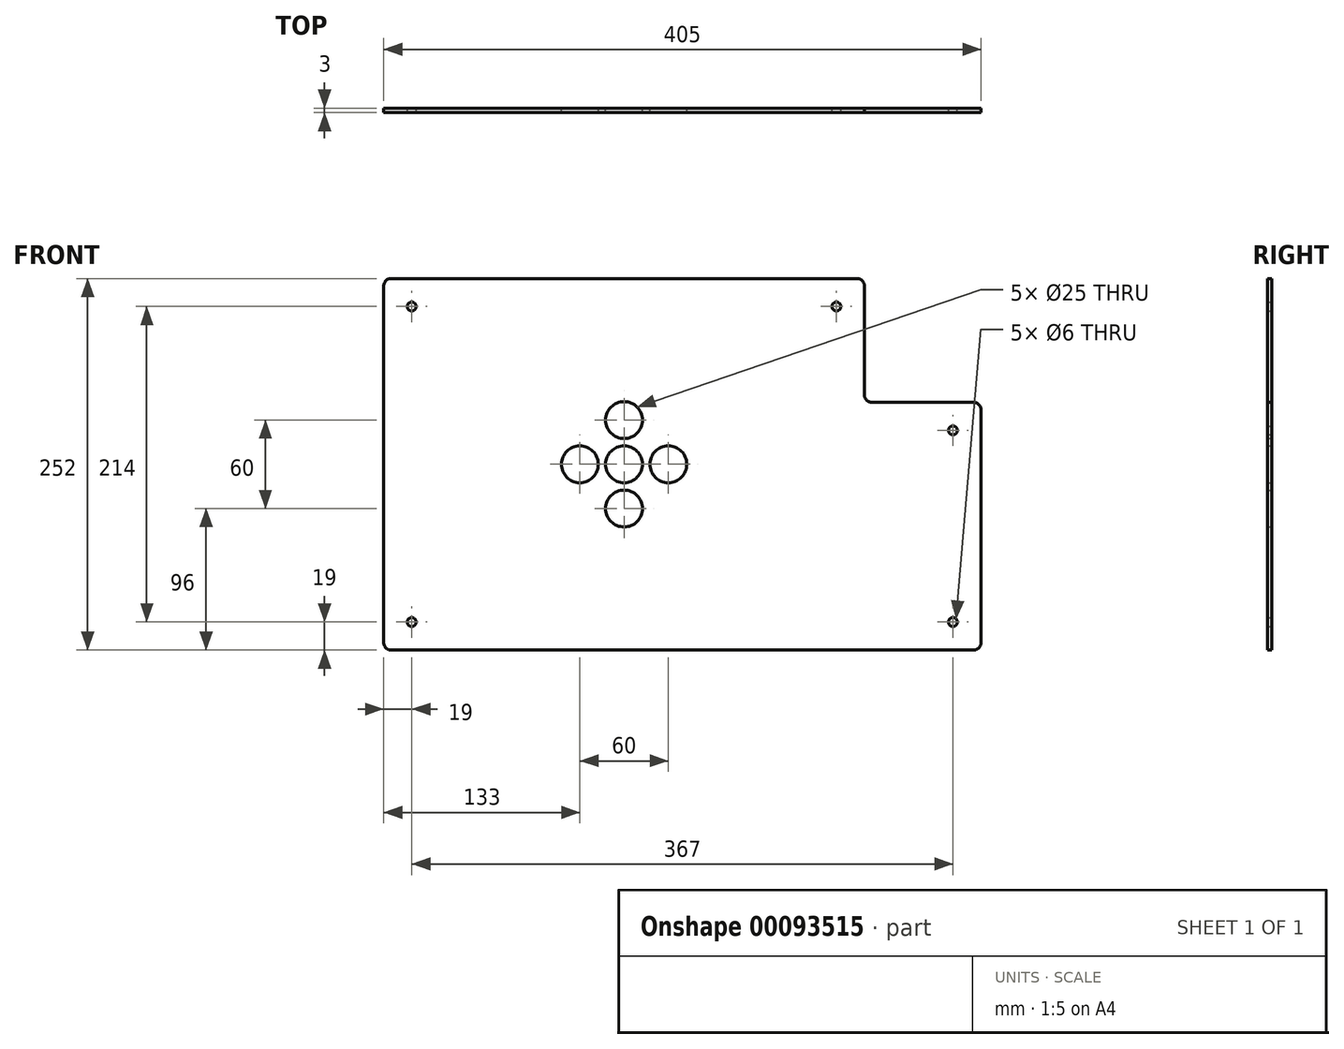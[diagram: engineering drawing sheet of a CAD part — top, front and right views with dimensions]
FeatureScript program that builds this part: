
annotation { "Feature Type Name" : "Feature", "Feature Type Description" : "" }
export const myFeature = defineFeature(function(context is Context, id is Id, definition is map)
    precondition{}
    {
        {
            var Q0;
            Q0=qCreatedBy(makeId("Front.planeOp"),FACE);
            var sketch = newSketch(context, id + "F0", { "sketchPlane" : qUnion([Q0])});
            skLineSegment(sketch, "E0", {"start": v(0, 0) * mm, "end": v(0, 252) * mm});
            skLineSegment(sketch, "E1", {"start": v(0, 0) * mm, "end": v(405, 0) * mm});
            skLineSegment(sketch, "E2", {"start": v(405, 0) * mm, "end": v(405, 168) * mm});
            skLineSegment(sketch, "E3", {"start": v(405, 168) * mm, "end": v(326, 168) * mm});
            skLineSegment(sketch, "E4", {"start": v(326, 168) * mm, "end": v(326, 252) * mm});
            skLineSegment(sketch, "E5", {"start": v(326, 252) * mm, "end": v(0, 252) * mm});
            skLineSegment(sketch, "E6", {"start": v(170.8, 252) * mm, "end": v(170.8, 233) * mm, "construction": true});
            skLineSegment(sketch, "E7", {"start": v(326, 210) * mm, "end": v(307, 210) * mm, "construction": true});
            skLineSegment(sketch, "E8", {"start": v(365.5, 168) * mm, "end": v(365.5, 149) * mm, "construction": true});
            skLineSegment(sketch, "E9", {"start": v(405, 62.88) * mm, "end": v(386, 62.88) * mm, "construction": true});
            skLineSegment(sketch, "E10", {"start": v(228.3, 0) * mm, "end": v(228.3, 19) * mm, "construction": true});
            skLineSegment(sketch, "E11", {"start": v(0, 112.37) * mm, "end": v(19, 112.37) * mm, "construction": true});
            skLineSegment(sketch, "E12", {"start": v(19, 112.37) * mm, "end": v(19, 233) * mm, "construction": true});
            skLineSegment(sketch, "E13", {"start": v(19, 233) * mm, "end": v(307, 233) * mm, "construction": true});
            skLineSegment(sketch, "E14", {"start": v(307, 233) * mm, "end": v(307, 149) * mm, "construction": true});
            skLineSegment(sketch, "E15", {"start": v(307, 149) * mm, "end": v(386, 149) * mm, "construction": true});
            skLineSegment(sketch, "E16", {"start": v(386, 149) * mm, "end": v(386, 19) * mm, "construction": true});
            skLineSegment(sketch, "E17", {"start": v(386, 19) * mm, "end": v(19, 19) * mm, "construction": true});
            skLineSegment(sketch, "E18", {"start": v(19, 19) * mm, "end": v(19, 112.37) * mm, "construction": true});
            skCircle(sketch, "E19", {"center": v(307, 233) * mm, "radius": 3 * mm});
            skCircle(sketch, "E20", {"center": v(19, 233) * mm, "radius": 3 * mm});
            skCircle(sketch, "E21", {"center": v(386, 149) * mm, "radius": 3 * mm});
            skCircle(sketch, "E22", {"center": v(19, 19) * mm, "radius": 3 * mm});
            skCircle(sketch, "E23", {"center": v(386, 19) * mm, "radius": 3 * mm});
            skLineSegment(sketch, "E24", {"start": v(163, 252) * mm, "end": v(163, 0) * mm, "construction": true});
            skLineSegment(sketch, "E25", {"start": v(163, 0) * mm, "end": v(158.03, 4.53) * mm, "construction": true});
            skLineSegment(sketch, "E26", {"start": v(0, 126) * mm, "end": v(405, 126) * mm, "construction": true});
            skLineSegment(sketch, "E27", {"start": v(405, 126) * mm, "end": v(409.35, 121.88) * mm, "construction": true});
            skCircle(sketch, "E28", {"center": v(163, 126) * mm, "radius": 12.5 * mm});
            skLineSegment(sketch, "E29", {"start": v(163, 126) * mm, "end": v(163, 156) * mm, "construction": true});
            skCircle(sketch, "E30", {"center": v(163, 156) * mm, "radius": 12.5 * mm});
            skLineSegment(sketch, "E31", {"start": v(163, 126) * mm, "end": v(163, 96) * mm, "construction": true});
            skLineSegment(sketch, "E32", {"start": v(163, 126) * mm, "end": v(193, 126) * mm, "construction": true});
            skLineSegment(sketch, "E33", {"start": v(163, 126) * mm, "end": v(133, 126) * mm, "construction": true});
            skCircle(sketch, "E34", {"center": v(133, 126) * mm, "radius": 12.5 * mm});
            skCircle(sketch, "E35", {"center": v(193, 126) * mm, "radius": 12.5 * mm});
            skCircle(sketch, "E36", {"center": v(163, 96) * mm, "radius": 12.5 * mm});
            skSolve(sketch);
        }
        {
            var Q0;
            Q0 = qSketchRegion(id + "F0", true);
            extrude(context, id + "F1", {"entities" : qUnion([Q0]), "depth" : 3 * mm});
        }
        {
            var Q0;
            Q0=makeQuery(id+"F1.opExtrude","SWEPT_EDGE",EDGE,{"disambiguationData":[OSD([sQuery(id+"F0.wireOp",EDGE,"E4"),sQuery(id+"F0.wireOp",EDGE,"E5")])]});
            var Q1;
            Q1=makeQuery(id+"F1.opExtrude","SWEPT_EDGE",EDGE,{"disambiguationData":[OSD([sQuery(id+"F0.wireOp",EDGE,"E2"),sQuery(id+"F0.wireOp",EDGE,"E3")])]});
            var Q2;
            Q2=makeQuery(id+"F1.opExtrude","SWEPT_EDGE",EDGE,{"disambiguationData":[OSD([sQuery(id+"F0.wireOp",EDGE,"E1"),sQuery(id+"F0.wireOp",EDGE,"E2")])]});
            var Q3;
            Q3=makeQuery(id+"F1.opExtrude","SWEPT_EDGE",EDGE,{"disambiguationData":[OSD([sQuery(id+"F0.wireOp",EDGE,"E0"),sQuery(id+"F0.wireOp",EDGE,"E1")])]});
            var Q4;
            Q4=makeQuery(id+"F1.opExtrude","SWEPT_EDGE",EDGE,{"disambiguationData":[OSD([sQuery(id+"F0.wireOp",EDGE,"E0"),sQuery(id+"F0.wireOp",EDGE,"E5")])]});
            fillet(context, id + "F2", {"entities" : qUnion([Q0, Q1, Q2, Q3, Q4]), "radius" : 5 * mm, "tangentPropagation" : true, "allowEdgeOverflow" : false});
        }
        {
            var Q0;
            Q0=makeQuery(id+"F1.opExtrude","SWEPT_EDGE",EDGE,{"disambiguationData":[OSD([sQuery(id+"F0.wireOp",EDGE,"E3"),sQuery(id+"F0.wireOp",EDGE,"E4")])]});
            fillet(context, id + "F3", {"entities" : qUnion([Q0]), "radius" : 5 * mm, "tangentPropagation" : true, "allowEdgeOverflow" : false});
        }
    });
